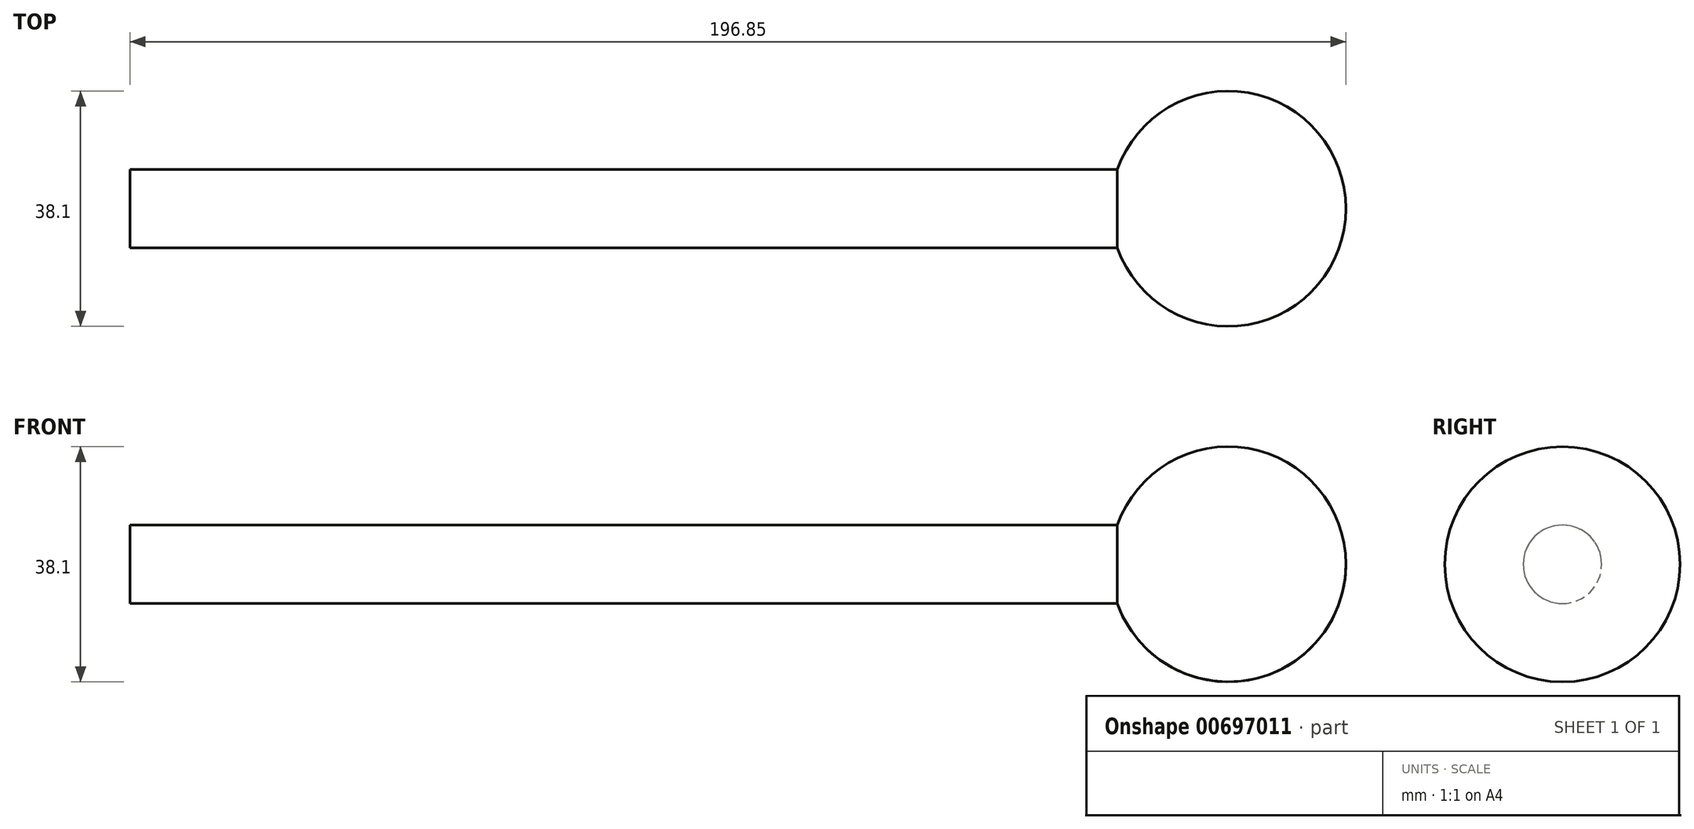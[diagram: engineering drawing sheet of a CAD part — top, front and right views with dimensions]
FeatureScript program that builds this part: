
annotation { "Feature Type Name" : "Feature", "Feature Type Description" : "" }
export const myFeature = defineFeature(function(context is Context, id is Id, definition is map)
    precondition{}
    {
        {
            var Q0;
            Q0=qCreatedBy(makeId("Front.planeOp"),FACE);
            var sketch = newSketch(context, id + "F0", { "sketchPlane" : qUnion([Q0])});
            skLineSegment(sketch, "E0.bottom", {"start": v(0, 0) * mm, "end": v(177.8, 0) * mm});
            skLineSegment(sketch, "E0.top", {"start": v(0, 6.35) * mm, "end": v(177.8, 6.35) * mm});
            skLineSegment(sketch, "E0.left", {"start": v(0, 0) * mm, "end": v(0, 6.35) * mm});
            skLineSegment(sketch, "E0.right", {"start": v(177.8, 0) * mm, "end": v(177.8, 6.35) * mm});
            skArc(sketch, "E1", {"start": v(158.75, 6.35) * mm, "mid": v(177.8, -12.7) * mm, "end": v(196.85, 6.35) * mm});
            skLineSegment(sketch, "E2", {"start": v(158.75, 6.35) * mm, "end": v(196.85, 6.35) * mm});
            skSolve(sketch);
        }
        {
            var Q0;
            Q0=qSketchRegion(id+"F0",true);
            var Q1;
            Q1=sQuery(id+"F0.wireOp",EDGE,"E0.top");
            revolve(context, id + "F1", {"entities" : qUnion([Q0]), "axis" : qUnion([Q1]), "revolveType" : RevolveType.FULL});
        }
    });
